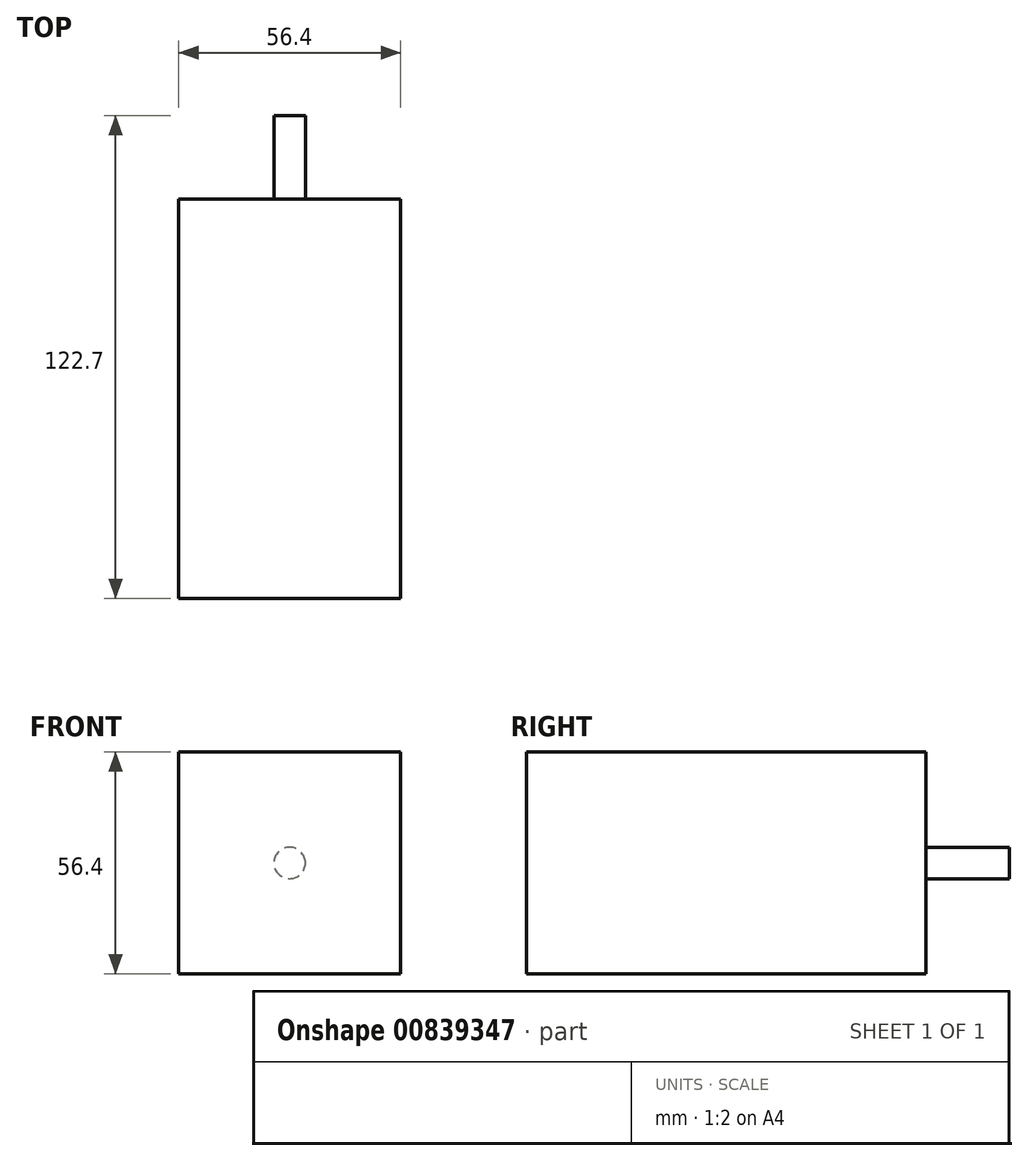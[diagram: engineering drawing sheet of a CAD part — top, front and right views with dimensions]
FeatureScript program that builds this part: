
annotation { "Feature Type Name" : "Feature", "Feature Type Description" : "" }
export const myFeature = defineFeature(function(context is Context, id is Id, definition is map)
    precondition{}
    {
        {
            var Q0;
            Q0=qCreatedBy(makeId("Front.planeOp"),FACE);
            var sketch = newSketch(context, id + "F0", { "sketchPlane" : qUnion([Q0])});
            skLineSegment(sketch, "E0", {"start": v(0, 33.45) * mm, "end": v(0, -44.25) * mm, "construction": true});
            skLineSegment(sketch, "E1", {"start": v(-42.45, 0) * mm, "end": v(44.06, 0) * mm, "construction": true});
            skLineSegment(sketch, "E2", {"start": v(-28.2, 0) * mm, "end": v(-28.2, 28.2) * mm});
            skLineSegment(sketch, "E3", {"start": v(-28.2, 28.2) * mm, "end": v(0, 28.2) * mm});
            skLineSegment(sketch, "E4.MirrorCS", {"start": v(28.2, 28.2) * mm, "end": v(0, 28.2) * mm});
            skLineSegment(sketch, "E5.MirrorCS", {"start": v(28.2, 0) * mm, "end": v(28.2, 28.2) * mm});
            skLineSegment(sketch, "E6.MirrorCS", {"start": v(-28.2, 0) * mm, "end": v(-28.2, -28.2) * mm});
            skLineSegment(sketch, "E7.MirrorCS", {"start": v(-28.2, -28.2) * mm, "end": v(0, -28.2) * mm});
            skLineSegment(sketch, "E8.MirrorCS", {"start": v(28.2, -28.2) * mm, "end": v(0, -28.2) * mm});
            skLineSegment(sketch, "E9.MirrorCS", {"start": v(28.2, 0) * mm, "end": v(28.2, -28.2) * mm});
            skSolve(sketch);
        }
        {
            var Q0;
            Q0=qSketchRegion(id+"F0",true);
            extrude(context, id + "F1", {"entities" : qUnion([Q0]), "depth" : 101.5 * mm, "offsetDistance" : 25 * mm});
        }
        {
            var Q0;
            Q0=makeQuery(id+"F1.opExtrude","CAP_FACE",FACE,{"disambiguationData":[OSD([sQuery(id+"F0.wireOp",EDGE,"E2"),sQuery(id+"F0.wireOp",EDGE,"E3"),sQuery(id+"F0.wireOp",EDGE,"E4.MirrorCS"),sQuery(id+"F0.wireOp",EDGE,"E5.MirrorCS"),sQuery(id+"F0.wireOp",EDGE,"E6.MirrorCS"),sQuery(id+"F0.wireOp",EDGE,"E7.MirrorCS"),sQuery(id+"F0.wireOp",EDGE,"E8.MirrorCS"),sQuery(id+"F0.wireOp",EDGE,"E9.MirrorCS")])],"isStart":true});
            var sketch = newSketch(context, id + "F2", { "sketchPlane" : qUnion([Q0])});
            skCircle(sketch, "E10", {"center": v(0, 0) * mm, "radius": 4 * mm});
            skSolve(sketch);
        }
        {
            var Q0;
            Q0=qSketchRegion(id+"F2",true);
            extrude(context, id + "F3", {"entities" : qUnion([Q0]), "operationType" : NewBodyOperationType.ADD, "depth" : 21.2 * mm, "offsetDistance" : 25 * mm});
        }
    });
